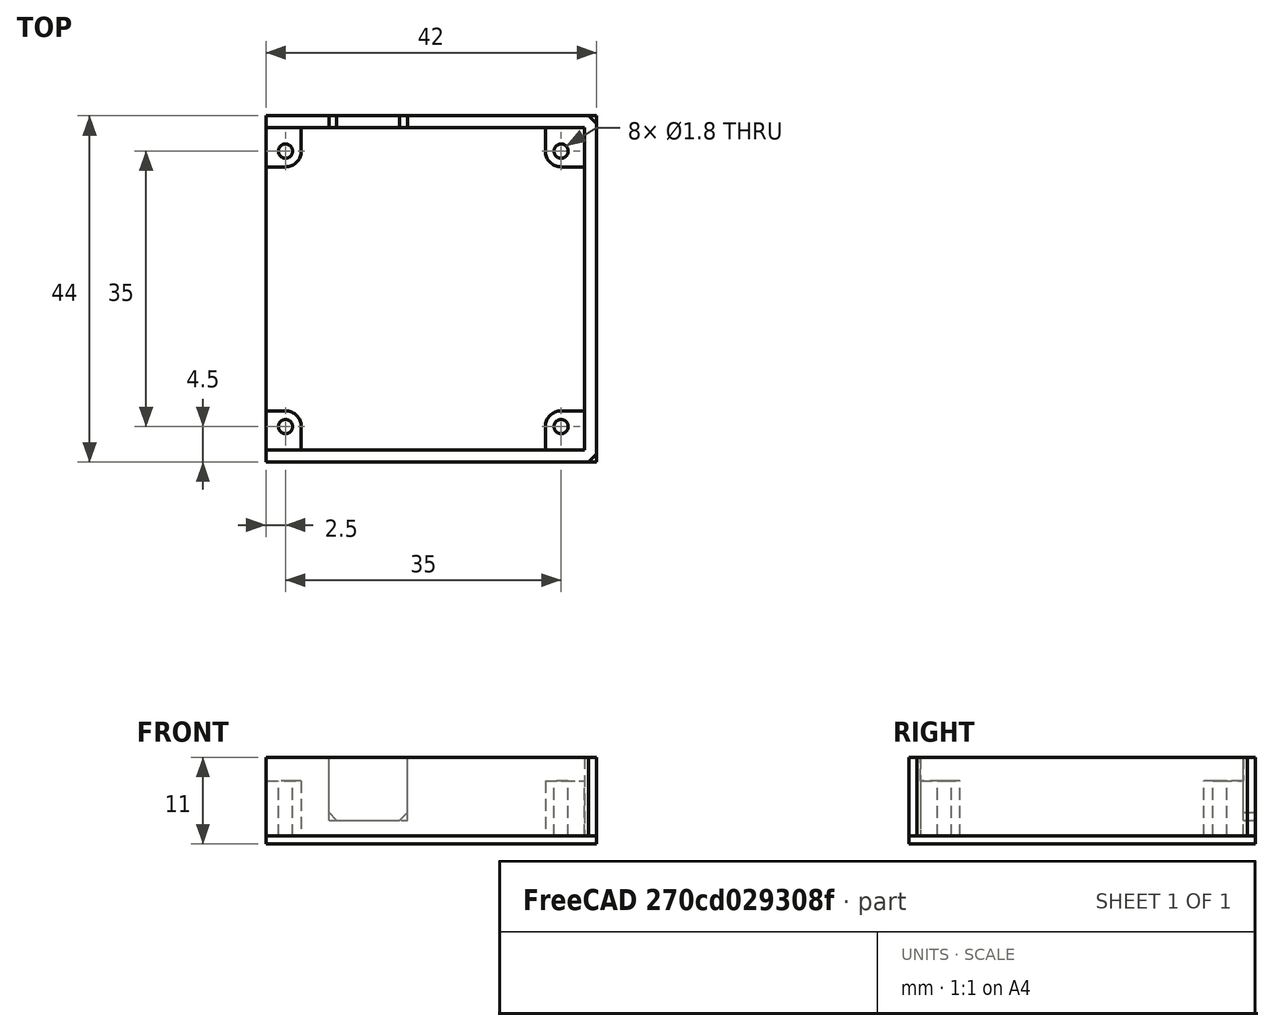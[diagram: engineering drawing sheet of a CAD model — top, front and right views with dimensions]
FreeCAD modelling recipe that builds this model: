
FCSTD DOCUMENT  (FreeCAD 0.18R14555 (Git shallow))
Label: 4010-blower-fan-mount
License: All rights reserved
LicenseURL: http://en.wikipedia.org/wiki/All_rights_reserved
objects: Part::Box×10, Part::Cylinder×4, Part::Fillet×4, Part::MultiFuse×3, Part::Feature×3, Part::Chamfer×2, Part::Cut×1
note: 27 computed .brp shape members not serialized (recipe doc carries the construction recipe); baked Part::Feature solids carry a one-line shape summary decoded from their .brp

FEATURE [Part::Box] Box  label="Cube"
  AttacherType = Attacher::AttachEngine3D
  Height = 1
  Length = 42
  Placement = pos=(-20,-22,-1) rot=(0,0,1;0rad)
  Width = 44
FEATURE [Part::Cylinder] Cylinder
  Angle = 360
  AttacherType = Attacher::AttachEngine3D
  Height = 10
  Placement = pos=(-17.5,17.5,0) rot=(0,0,1;0rad)
  Radius = 0.9
FEATURE [Part::Cylinder] Cylinder001
  Angle = 360
  AttacherType = Attacher::AttachEngine3D
  Height = 10
  Placement = pos=(17.5,17.5,0) rot=(0,0,1;0rad)
  Radius = 0.9
FEATURE [Part::Cylinder] Cylinder002
  Angle = 360
  AttacherType = Attacher::AttachEngine3D
  Height = 10
  Placement = pos=(-17.5,-17.5,0) rot=(0,0,1;0rad)
  Radius = 0.9
FEATURE [Part::Cylinder] Cylinder003
  Angle = 360
  AttacherType = Attacher::AttachEngine3D
  Height = 10
  Placement = pos=(17.5,-17.5,0) rot=(0,0,1;0rad)
  Radius = 0.9
FEATURE [Part::Box] Box003  label="Cube003"
  AttacherType = Attacher::AttachEngine3D
  Height = 7
  Length = 4.5
  Placement = pos=(-20,15.5,0) rot=(0,0,1;0rad)
  Width = 5.5
FEATURE [Part::Box] Box004  label="Cube004"
  AttacherType = Attacher::AttachEngine3D
  Height = 7
  Length = 5.5
  Placement = pos=(15.5,15.5,0) rot=(0,0,1;0rad)
  Width = 5.5
FEATURE [Part::Box] Box005  label="Cube005"
  AttacherType = Attacher::AttachEngine3D
  Height = 7
  Length = 4.5
  Placement = pos=(-20,-21,0) rot=(0,0,1;0rad)
  Width = 5.5
FEATURE [Part::Box] Box006  label="Cube006"
  AttacherType = Attacher::AttachEngine3D
  Height = 7
  Length = 5.5
  Placement = pos=(15.5,-21,0) rot=(0,0,1;0rad)
  Width = 5.5
FEATURE [Part::Box] Box007  label="Cube007"
  AttacherType = Attacher::AttachEngine3D
  Height = 10
  Length = 42
  Placement = pos=(-20,-22,0) rot=(0,0,1;0rad)
  Width = 1.5
FEATURE [Part::Box] Box008  label="Cube008"
  AttacherType = Attacher::AttachEngine3D
  Height = 10
  Length = 8
  Placement = pos=(-20,20.5,0) rot=(0,0,1;0rad)
  Width = 1.5
FEATURE [Part::MultiFuse] Fusion
  Shapes = -> [Cylinder003,Cylinder,Cylinder002,Cylinder001]
FEATURE [Part::Box] Box009  label="Cube009"
  AttacherType = Attacher::AttachEngine3D
  Height = 10
  Length = 1.5
  Placement = pos=(20.5,-22,0) rot=(0,0,1;0rad)
  Width = 44
FEATURE [Part::Box] Box010  label="Cube010"
  AttacherType = Attacher::AttachEngine3D
  Height = 10
  Length = 24
  Placement = pos=(-2,20.5,0) rot=(0,0,1;0rad)
  Width = 1.5
FEATURE [Part::Fillet] Fillet
  Base = -> Box003
  Edges = 1 edges r=2: [Edge5]
FEATURE [Part::Fillet] Fillet001
  Base = -> Box004
  Edges = 1 edges r=2: [Edge1]
FEATURE [Part::Fillet] Fillet002
  Base = -> Box006
  Edges = 1 edges r=2: [Edge3]
FEATURE [Part::Fillet] Fillet003
  Base = -> Box005
  Edges = 1 edges r=2: [Edge7]
FEATURE [Part::Box] Box011  label="Cube011"
  AttacherType = Attacher::AttachEngine3D
  Height = 2
  Length = 10
  Placement = pos=(-12,20.5,0) rot=(0,0,1;0rad)
  Width = 1.5
FEATURE [Part::MultiFuse] Fusion001
  Shapes = -> [Box008,Box010,Box011,Box007,Box009]
FEATURE [Part::Feature] Fusion001001  label="Fusion002"
  shape: bbox 42 x 44 x 10 mm, 14 faces (baked)
FEATURE [Part::Chamfer] Chamfer
  Base = -> Fusion001001
  Edges = 2 edges r=1: [Edge24,Edge26]
FEATURE [Part::Chamfer] Chamfer001
  Base = -> Chamfer
  Edges = 2 edges r=1: [Edge39,Edge42]
FEATURE [Part::MultiFuse] Fusion001002
  Shapes = -> [Chamfer001,Fillet003,Fillet002,Fillet001,Fillet]
FEATURE [Part::Cut] Cut
  Base = -> Fusion001002
  Tool = -> Fusion
FEATURE [Part::Feature] Cut001
  shape: bbox 42 x 44 x 10 mm, 38 faces (baked)
FEATURE [Part::Feature] Cut001_solid  label="Cut001 (Solid)"
  shape: bbox 42 x 44 x 10 mm, 38 faces (baked)
